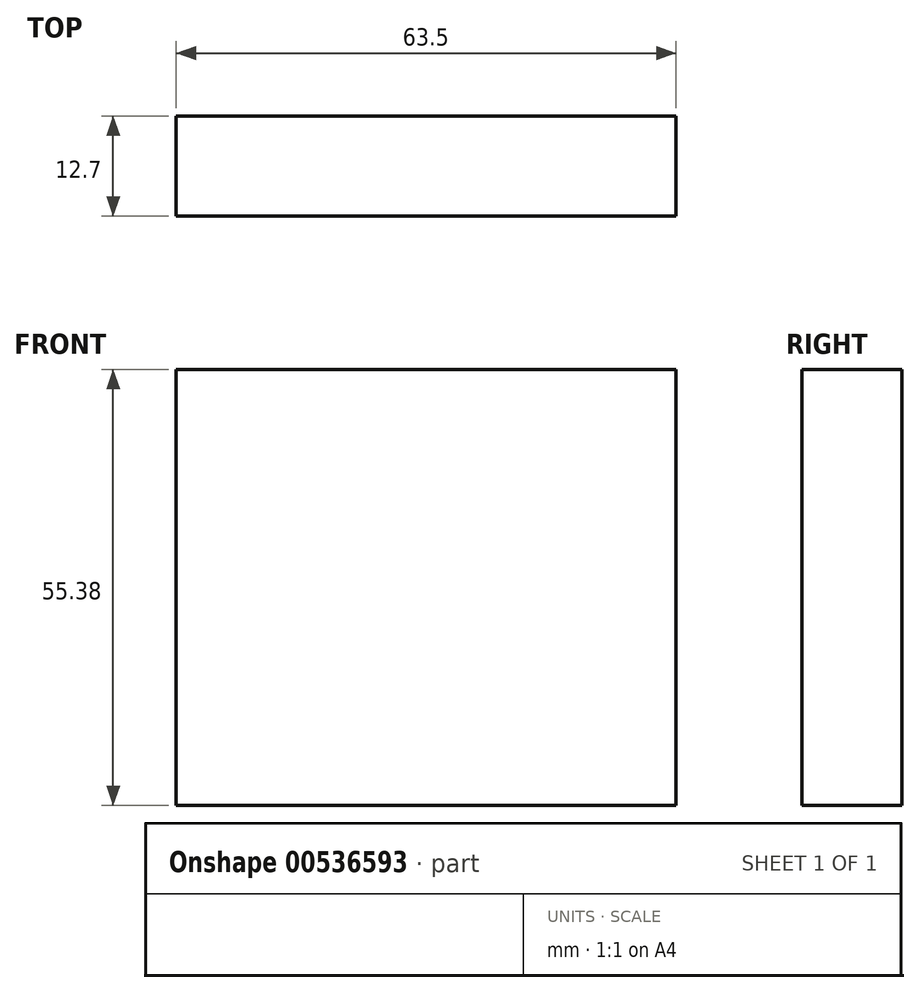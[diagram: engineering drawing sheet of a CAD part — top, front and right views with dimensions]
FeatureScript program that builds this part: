
annotation { "Feature Type Name" : "Feature", "Feature Type Description" : "" }
export const myFeature = defineFeature(function(context is Context, id is Id, definition is map)
    precondition{}
    {
        {
            var Q0;
            Q0=qCreatedBy(makeId("Front.planeOp"),FACE);
            var sketch = newSketch(context, id + "F0", { "sketchPlane" : qUnion([Q0])});
            skLineSegment(sketch, "E0.bottom", {"start": v(-33.14, 25.69) * mm, "end": v(30.36, 25.69) * mm});
            skLineSegment(sketch, "E0.top", {"start": v(-33.14, -29.69) * mm, "end": v(30.36, -29.69) * mm});
            skLineSegment(sketch, "E0.left", {"start": v(-33.14, 25.69) * mm, "end": v(-33.14, -29.69) * mm});
            skLineSegment(sketch, "E0.right", {"start": v(30.36, 25.69) * mm, "end": v(30.36, -29.69) * mm});
            skSolve(sketch);
        }
        {
            var Q0;
            Q0 = qSketchRegion(id + "F0", true);
            extrude(context, id + "F1", {"entities" : qUnion([Q0]), "depth" : 12.7 * mm, "offsetDistance" : 25.4 * mm});
        }
    });
